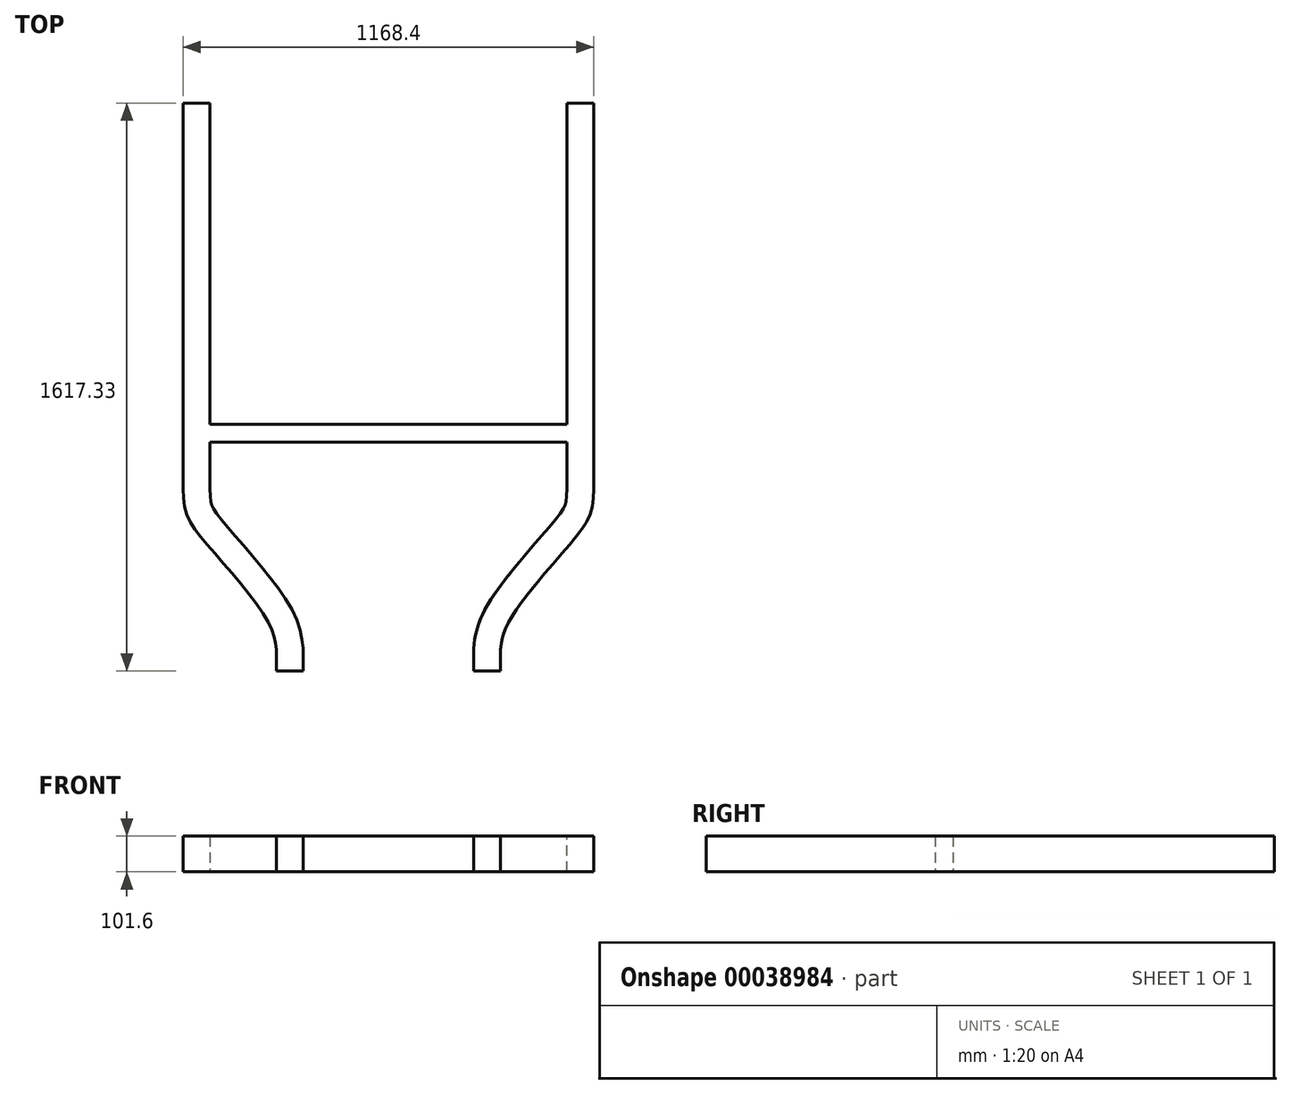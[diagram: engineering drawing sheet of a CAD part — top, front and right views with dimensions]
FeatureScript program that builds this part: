
annotation { "Feature Type Name" : "Feature", "Feature Type Description" : "" }
export const myFeature = defineFeature(function(context is Context, id is Id, definition is map)
    precondition{}
    {
        {
            var Q0;
            Q0=qCreatedBy(makeId("Front.planeOp"),FACE);
            var sketch = newSketch(context, id + "F0", { "sketchPlane" : qUnion([Q0])});
            skLineSegment(sketch, "E0.bottom", {"start": v(-584.2, 0) * mm, "end": v(-508, 0) * mm});
            skLineSegment(sketch, "E0.top", {"start": v(-584.2, -101.6) * mm, "end": v(-508, -101.6) * mm});
            skLineSegment(sketch, "E0.left", {"start": v(-584.2, 0) * mm, "end": v(-584.2, -101.6) * mm});
            skLineSegment(sketch, "E0.right", {"start": v(-508, 0) * mm, "end": v(-508, -101.6) * mm});
            skSolve(sketch);
        }
        {
            var Q0;
            Q0 = qSketchRegion(id + "F0", true);
            extrude(context, id + "F1", {"entities" : qUnion([Q0]), "depth" : 304.8 * mm, "hasSecondDirection" : true, "secondDirectionOppositeDirection" : true, "secondDirectionDepth" : 762 * mm});
        }
        {
            var Q0;
            Q0=qCreatedBy(makeId("Top.planeOp"),FACE);
            var sketch = newSketch(context, id + "F2", { "sketchPlane" : qUnion([Q0])});
            skFitSpline(sketch, "E1", {"points": [v(-546.82, -304.76) * mm, v(-517, -433.67) * mm, v(-303.85, -708.41) * mm, v(-281.6, -855.2) * mm], "startDerivative": vector(0.06, -804.72) * mm, "endDerivative": vector(1.69, -489.3) * mm});
            skSolve(sketch);
        }
        {
            var Q0;
            Q0=makeQuery(id+"F1.opExtrude","CAP_FACE",FACE,{"disambiguationData":[OSD([sQuery(id+"F0.wireOp",EDGE,"E0.bottom"),sQuery(id+"F0.wireOp",EDGE,"E0.top"),sQuery(id+"F0.wireOp",EDGE,"E0.left"),sQuery(id+"F0.wireOp",EDGE,"E0.right")])],"isStart":false});
            var Q1;
            Q1=sQuery(id+"F2.wireOp",EDGE,"E1");
            sweep(context, id + "F3", {"operationType" : NewBodyOperationType.ADD, "profiles" : qUnion([Q0]), "path" : qUnion([Q1])});
        }
        {
            var Q0;
            Q0=makeQuery(id+"F1.opExtrude","SWEPT_BODY",BODY,{"disambiguationData":[OSD([sQuery(id+"F0.wireOp",EDGE,"E0.bottom"),sQuery(id+"F0.wireOp",EDGE,"E0.top"),sQuery(id+"F0.wireOp",EDGE,"E0.left"),sQuery(id+"F0.wireOp",EDGE,"E0.right")])]});
            var Q1;
            Q1=qCreatedBy(makeId("Right.planeOp"),FACE);
            mirror(context, id + "F4", {"entities" : qUnion([Q0]), "mirrorPlane" : qUnion([Q1])});
        }
        {
            var Q0;
            Q0=makeQuery(id+"F1.opExtrude","SWEPT_FACE",FACE,{"disambiguationData":[OSD([sQuery(id+"F0.wireOp",EDGE,"E0.right")])]});
            var sketch = newSketch(context, id + "F5", { "sketchPlane" : qUnion([Q0])});
            skLineSegment(sketch, "E2.bottom", {"start": v(-203.2, 0) * mm, "end": v(-152.4, 0) * mm});
            skLineSegment(sketch, "E2.top", {"start": v(-203.2, -101.6) * mm, "end": v(-152.4, -101.6) * mm});
            skLineSegment(sketch, "E2.left", {"start": v(-203.2, 0) * mm, "end": v(-203.2, -101.6) * mm});
            skLineSegment(sketch, "E2.right", {"start": v(-152.4, 0) * mm, "end": v(-152.4, -101.6) * mm});
            skSolve(sketch);
        }
        {
            var Q0;
            Q0 = qSketchRegion(id + "F5", true);
            extrude(context, id + "F6", {"entities" : qUnion([Q0]), "operationType" : NewBodyOperationType.ADD, "endBound" : BoundingType.UP_TO_NEXT, "depth" : 946.77 * mm});
        }
    });
